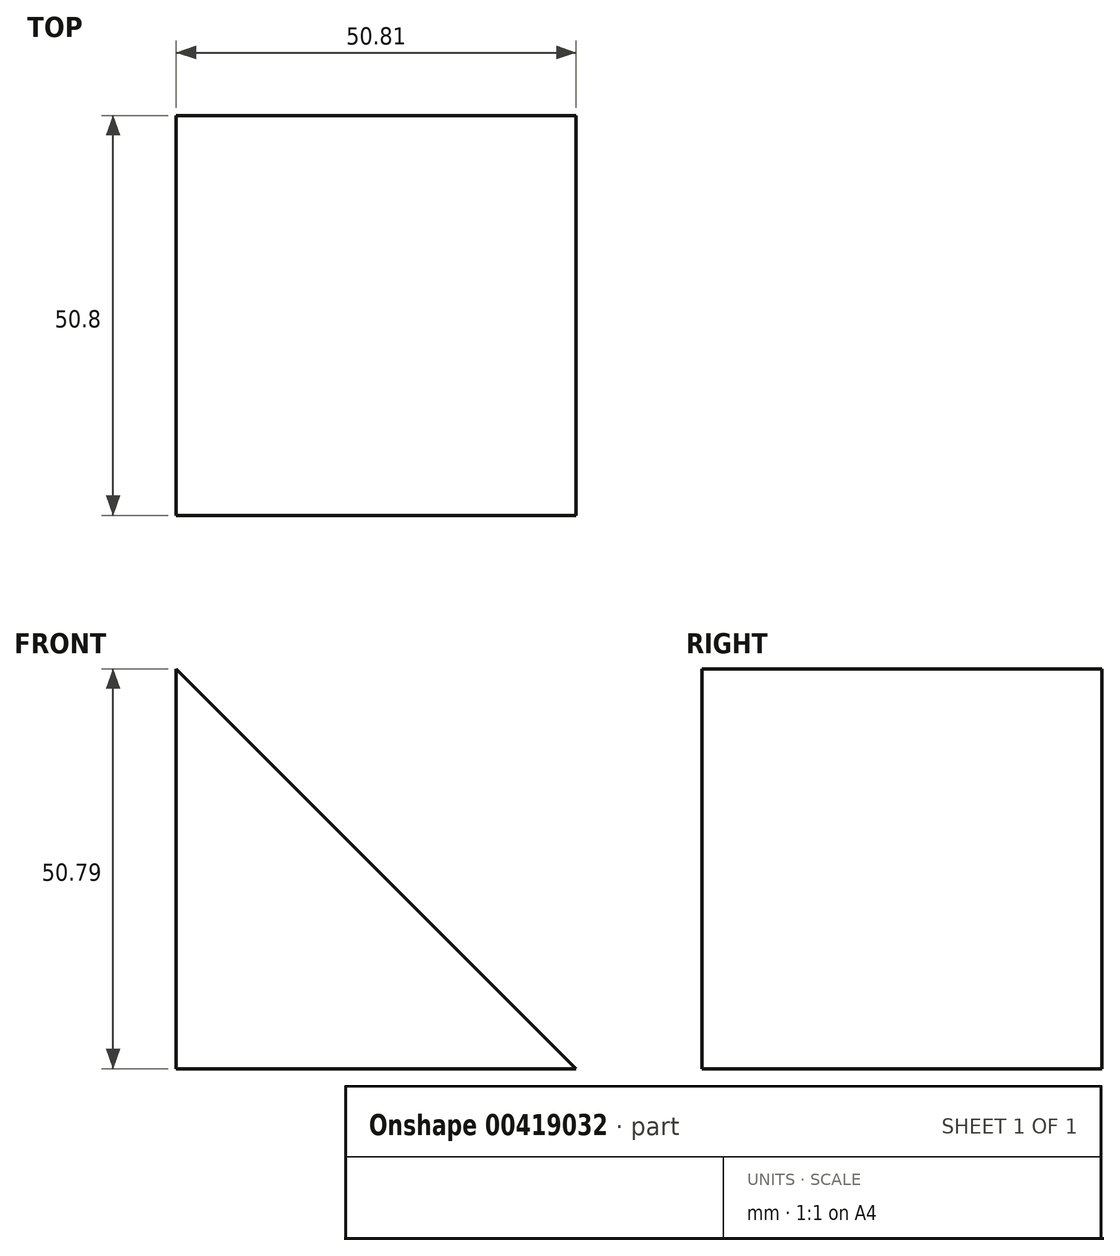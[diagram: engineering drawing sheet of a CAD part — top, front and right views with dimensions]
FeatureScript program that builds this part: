
annotation { "Feature Type Name" : "Feature", "Feature Type Description" : "" }
export const myFeature = defineFeature(function(context is Context, id is Id, definition is map)
    precondition{}
    {
        {
            var Q0;
            Q0=qCreatedBy(makeId("Front.planeOp"),FACE);
            var sketch = newSketch(context, id + "F0", { "sketchPlane" : qUnion([Q0])});
            skLineSegment(sketch, "E0", {"start": v(0, 0) * mm, "end": v(-50.81, 0) * mm});
            skLineSegment(sketch, "E1", {"start": v(-50.81, 0) * mm, "end": v(-50.81, 50.79) * mm});
            skLineSegment(sketch, "E2", {"start": v(0, 0) * mm, "end": v(-50.81, 50.79) * mm});
            skPoint(sketch, "E3.start.orphan", {"position": v(0, 50.79) * mm});
            skSolve(sketch);
        }
        {
            var Q0;
            Q0=makeQuery(id+"F0.imprint","IMPRINT",FACE,{"disambiguationData":[TD([[makeQuery(id+"F0.imprint","IMPRINT",EDGE,{"derivedFrom":sQuery(id+"F0.wireOp",EDGE,"E0")}),-1.0]])]});
            extrude(context, id + "F1", {"entities" : qUnion([Q0]), "depth" : 50.8 * mm});
        }
    });
